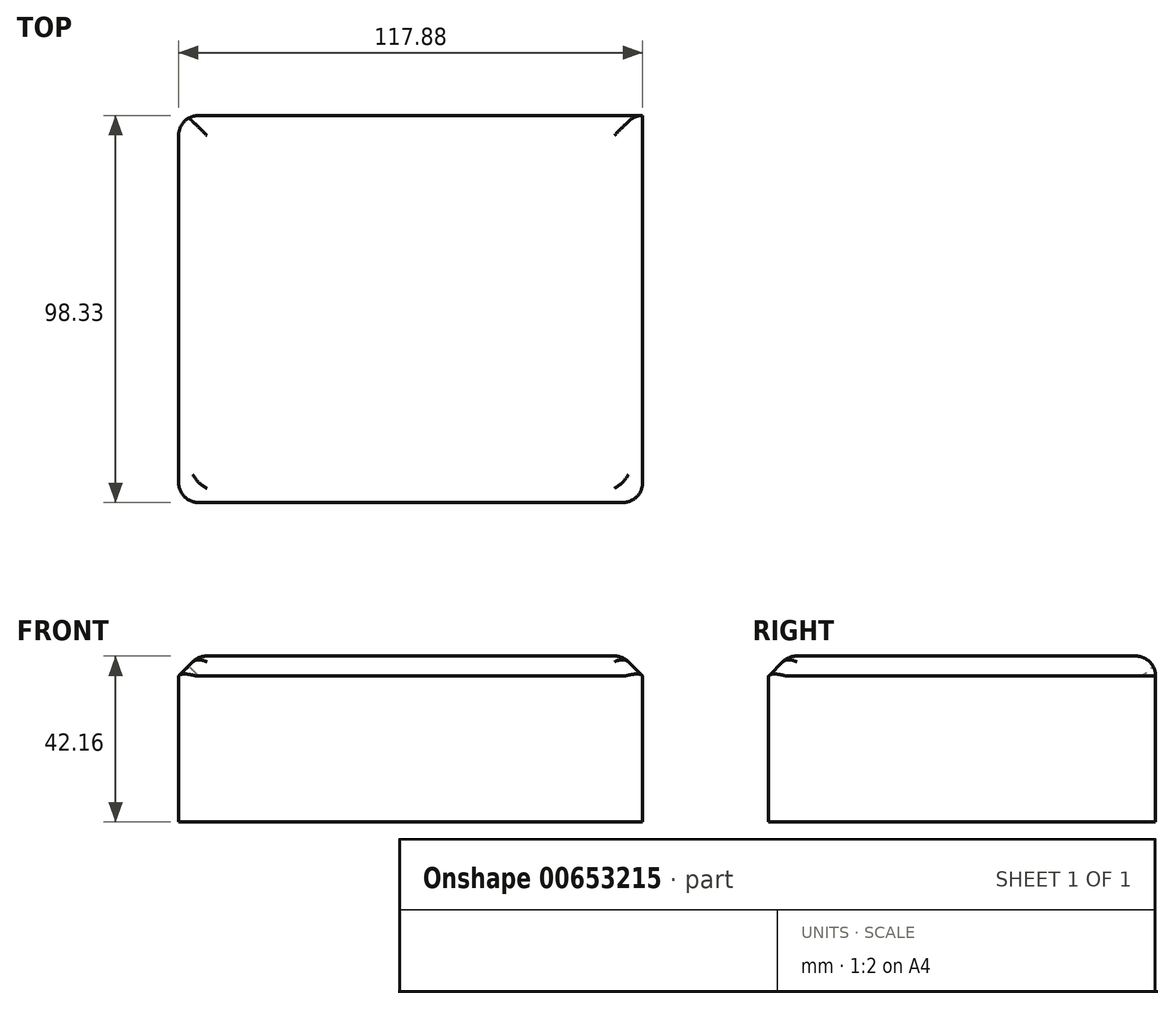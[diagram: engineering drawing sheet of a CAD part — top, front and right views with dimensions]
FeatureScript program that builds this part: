
annotation { "Feature Type Name" : "Feature", "Feature Type Description" : "" }
export const myFeature = defineFeature(function(context is Context, id is Id, definition is map)
    precondition{}
    {
        {
            var Q0;
            Q0=qCreatedBy(makeId("Top.planeOp"),FACE);
            var sketch = newSketch(context, id + "F0", { "sketchPlane" : qUnion([Q0])});
            skLineSegment(sketch, "E0.bottom", {"start": v(-61.38, -40) * mm, "end": v(56.5, -40) * mm});
            skLineSegment(sketch, "E0.top", {"start": v(-61.38, 58.34) * mm, "end": v(56.5, 58.34) * mm});
            skLineSegment(sketch, "E0.left", {"start": v(-61.38, -40) * mm, "end": v(-61.38, 58.34) * mm});
            skLineSegment(sketch, "E0.right", {"start": v(56.5, -40) * mm, "end": v(56.5, 58.34) * mm});
            skSolve(sketch);
        }
        {
            var Q0;
            Q0 = qSketchRegion(id + "F0", true);
            extrude(context, id + "F1", {"entities" : qUnion([Q0]), "depth" : 42.16 * mm, "offsetDistance" : 25.4 * mm});
        }
        {
            var Q0;
            Q0=makeQuery(id+"F1.opExtrude","CAP_EDGE",EDGE,{"disambiguationData":[OSD([sQuery(id+"F0.wireOp",EDGE,"E0.bottom")])],"isStart":false});
            var Q1;
            Q1=makeQuery(id+"F1.opExtrude","CAP_EDGE",EDGE,{"disambiguationData":[OSD([sQuery(id+"F0.wireOp",EDGE,"E0.left")])],"isStart":false});
            var Q2;
            Q2=makeQuery(id+"F1.opExtrude","CAP_EDGE",EDGE,{"disambiguationData":[OSD([sQuery(id+"F0.wireOp",EDGE,"E0.right")])],"isStart":false});
            chamfer(context, id + "F2", {"entities" : qUnion([Q0, Q1, Q2]), "width" : 5.08 * mm, "tangentPropagation" : true});
        }
        {
            var Q0;
            Q0=makeQuery(id+"F1.opExtrude","SWEPT_EDGE",EDGE,{"disambiguationData":[OSD([sQuery(id+"F0.wireOp",EDGE,"E0.bottom"),sQuery(id+"F0.wireOp",EDGE,"E0.right")])]});
            var Q1;
            Q1=makeQuery(id+"F2.opChamfer","BLEND_EDGE",EDGE,{"blendedFrom":[makeQuery(id+"F1.opExtrude","CAP_EDGE",EDGE,{"disambiguationData":[OSD([sQuery(id+"F0.wireOp",EDGE,"E0.bottom")])],"isStart":false}),makeQuery(id+"F1.opExtrude","CAP_EDGE",EDGE,{"disambiguationData":[OSD([sQuery(id+"F0.wireOp",EDGE,"E0.right")])],"isStart":false})],"blendedInto":[]});
            var Q2;
            {var subQ0=sQuery(id+"F0.wireOp",EDGE,"E0.right");Q2=makeQuery(id+"F2.opChamfer","BLEND_EDGE",EDGE,{"blendedFrom":[makeQuery(id+"F1.opExtrude","CAP_EDGE",EDGE,{"disambiguationData":[OSD([subQ0])],"isStart":false}),makeQuery(id+"F1.opExtrude","CAP_FACE",FACE,{"disambiguationData":[OSD([sQuery(id+"F0.wireOp",EDGE,"E0.bottom"),sQuery(id+"F0.wireOp",EDGE,"E0.top"),sQuery(id+"F0.wireOp",EDGE,"E0.left"),subQ0])],"isStart":false})],"blendedInto":[makeQuery(id+"F1.opExtrude","CAP_FACE",FACE,{"disambiguationData":[OSD([sQuery(id+"F0.wireOp",EDGE,"E0.bottom"),sQuery(id+"F0.wireOp",EDGE,"E0.top"),sQuery(id+"F0.wireOp",EDGE,"E0.left"),subQ0])],"isStart":false})]});}
            var Q3;
            {var subQ0=sQuery(id+"F0.wireOp",EDGE,"E0.bottom");Q3=makeQuery(id+"F2.opChamfer","BLEND_EDGE",EDGE,{"blendedFrom":[makeQuery(id+"F1.opExtrude","CAP_EDGE",EDGE,{"disambiguationData":[OSD([subQ0])],"isStart":false}),makeQuery(id+"F1.opExtrude","CAP_FACE",FACE,{"disambiguationData":[OSD([subQ0,sQuery(id+"F0.wireOp",EDGE,"E0.top"),sQuery(id+"F0.wireOp",EDGE,"E0.left"),sQuery(id+"F0.wireOp",EDGE,"E0.right")])],"isStart":false})],"blendedInto":[makeQuery(id+"F1.opExtrude","CAP_FACE",FACE,{"disambiguationData":[OSD([subQ0,sQuery(id+"F0.wireOp",EDGE,"E0.top"),sQuery(id+"F0.wireOp",EDGE,"E0.left"),sQuery(id+"F0.wireOp",EDGE,"E0.right")])],"isStart":false})]});}
            var Q4;
            Q4=makeQuery(id+"F2.opChamfer","BLEND_EDGE",EDGE,{"blendedFrom":[makeQuery(id+"F1.opExtrude","CAP_EDGE",EDGE,{"disambiguationData":[OSD([sQuery(id+"F0.wireOp",EDGE,"E0.bottom")])],"isStart":false}),makeQuery(id+"F1.opExtrude","CAP_EDGE",EDGE,{"disambiguationData":[OSD([sQuery(id+"F0.wireOp",EDGE,"E0.left")])],"isStart":false})],"blendedInto":[]});
            var Q5;
            Q5=makeQuery(id+"F1.opExtrude","SWEPT_EDGE",EDGE,{"disambiguationData":[OSD([sQuery(id+"F0.wireOp",EDGE,"E0.bottom"),sQuery(id+"F0.wireOp",EDGE,"E0.left")])]});
            var Q6;
            Q6=makeQuery(id+"F1.opExtrude","SWEPT_EDGE",EDGE,{"disambiguationData":[OSD([sQuery(id+"F0.wireOp",EDGE,"E0.top"),sQuery(id+"F0.wireOp",EDGE,"E0.left")])]});
            var Q7;
            Q7=makeQuery(id+"F1.opExtrude","CAP_EDGE",EDGE,{"disambiguationData":[OSD([sQuery(id+"F0.wireOp",EDGE,"E0.top")])],"isStart":false});
            var Q8;
            {var subQ0=sQuery(id+"F0.wireOp",EDGE,"E0.left");Q8=makeQuery(id+"F2.opChamfer","BLEND_EDGE",EDGE,{"blendedFrom":[makeQuery(id+"F1.opExtrude","CAP_EDGE",EDGE,{"disambiguationData":[OSD([subQ0])],"isStart":false}),makeQuery(id+"F1.opExtrude","CAP_FACE",FACE,{"disambiguationData":[OSD([sQuery(id+"F0.wireOp",EDGE,"E0.bottom"),sQuery(id+"F0.wireOp",EDGE,"E0.top"),subQ0,sQuery(id+"F0.wireOp",EDGE,"E0.right")])],"isStart":false})],"blendedInto":[makeQuery(id+"F1.opExtrude","CAP_FACE",FACE,{"disambiguationData":[OSD([sQuery(id+"F0.wireOp",EDGE,"E0.bottom"),sQuery(id+"F0.wireOp",EDGE,"E0.top"),subQ0,sQuery(id+"F0.wireOp",EDGE,"E0.right")])],"isStart":false})]});}
            fillet(context, id + "F3", {"entities" : qUnion([Q0, Q1, Q2, Q3, Q4, Q5, Q6, Q7, Q8]), "radius" : 5.08 * mm, "tangentPropagation" : true, "allowEdgeOverflow" : false});
        }
    });
